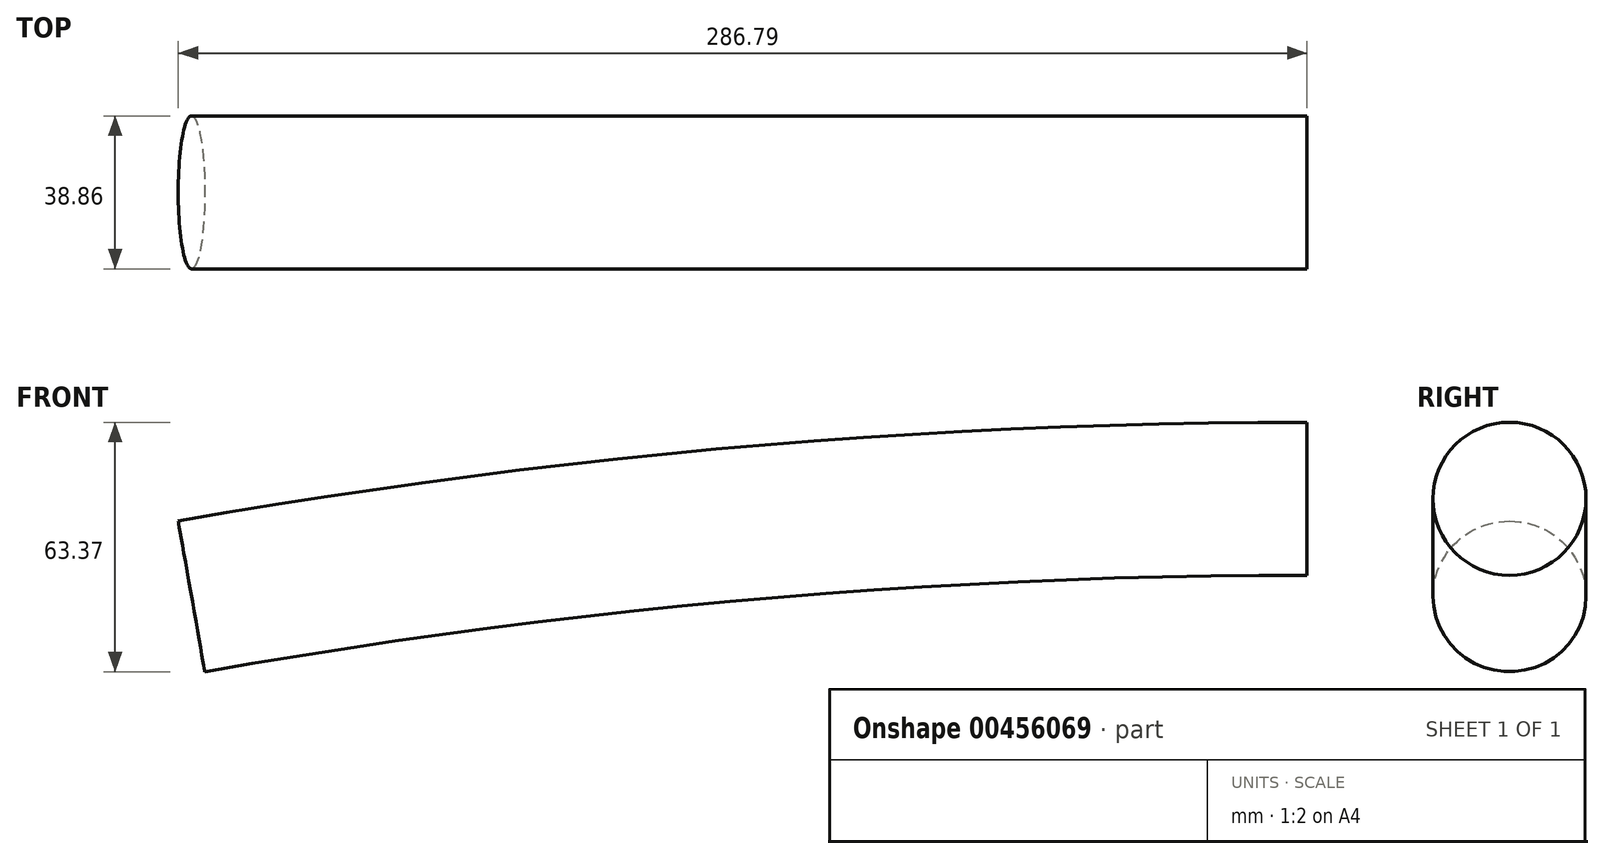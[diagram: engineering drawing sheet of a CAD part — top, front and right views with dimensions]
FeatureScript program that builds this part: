
annotation { "Feature Type Name" : "Feature", "Feature Type Description" : "" }
export const myFeature = defineFeature(function(context is Context, id is Id, definition is map)
    precondition{}
    {
        {
            var Q0;
            Q0=qCreatedBy(makeId("Top.planeOp"),FACE);
            var sketch = newSketch(context, id + "F0", { "sketchPlane" : qUnion([Q0])});
            skLineSegment(sketch, "E0", {"start": v(0, 0) * mm, "end": v(1632.15, 0) * mm});
            skCircle(sketch, "E1", {"center": v(1632.15, 0) * mm, "radius": 19.43 * mm});
            skLineSegment(sketch, "E2", {"start": v(0, 18.17) * mm, "end": v(0, -26.19) * mm});
            skSolve(sketch);
        }
        {
            var Q0;
            Q0=makeQuery(id+"F0.imprint","IMPRINT",FACE,{"disambiguationData":[TD([[makeQuery(id+"F0.imprint","IMPRINT",EDGE,{"derivedFrom":sQuery(id+"F0.wireOp",EDGE,"E1")}),1.0]])]});
            var Q1;
            Q1=sQuery(id+"F0.wireOp",EDGE,"E2");
            revolve(context, id + "F1", {"entities" : qUnion([Q0]), "axis" : qUnion([Q1]), "revolveType" : RevolveType.TWO_DIRECTIONS, "oppositeDirection" : true, "angle" : 270 * degree, "angleBack" : 260 * degree});
        }
    });
